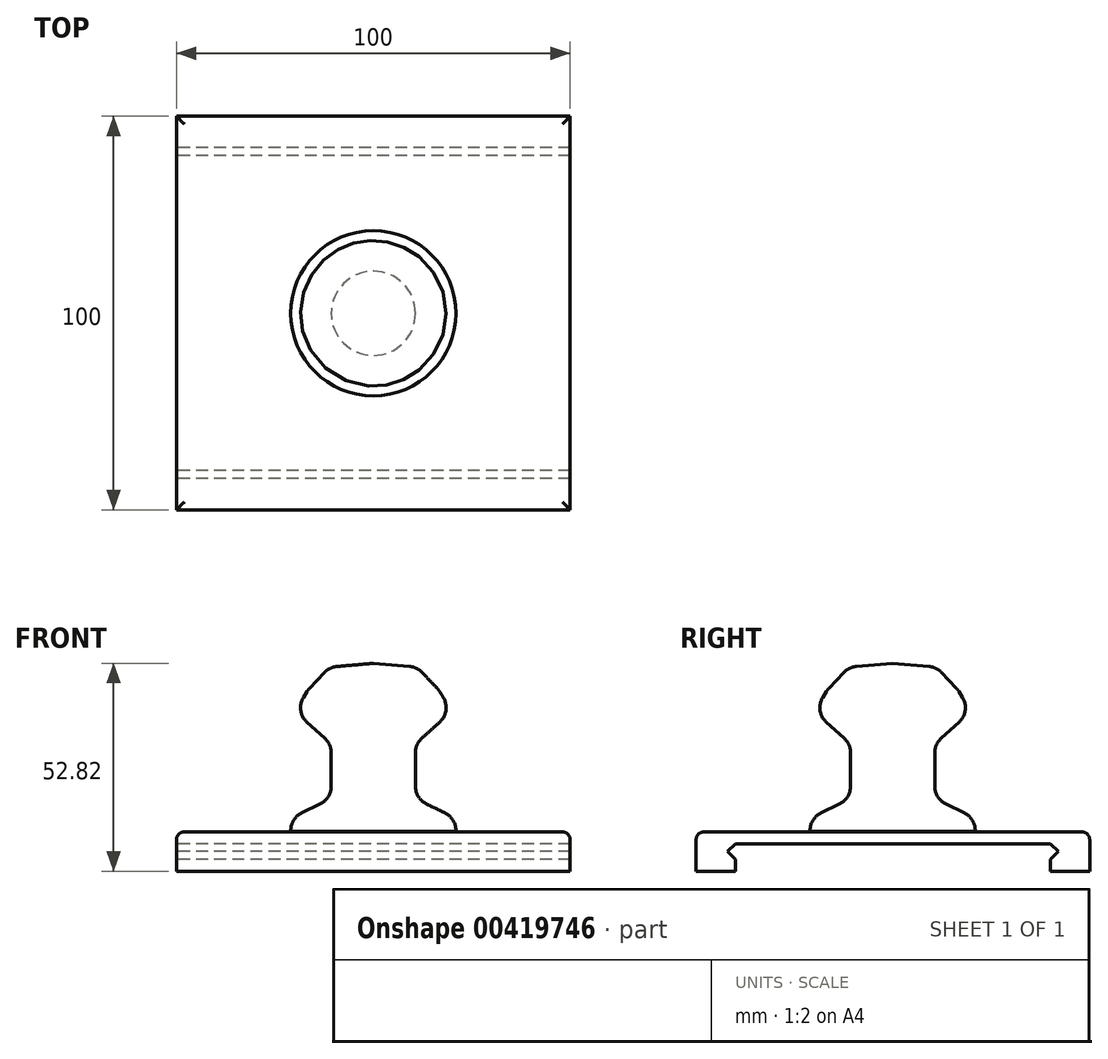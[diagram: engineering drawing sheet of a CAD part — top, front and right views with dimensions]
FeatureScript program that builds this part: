
annotation { "Feature Type Name" : "Feature", "Feature Type Description" : "" }
export const myFeature = defineFeature(function(context is Context, id is Id, definition is map)
    precondition{}
    {
        {
            var Q0;
            Q0=qCreatedBy(makeId("Right.planeOp"),FACE);
            var sketch = newSketch(context, id + "F0", { "sketchPlane" : qUnion([Q0])});
            skLineSegment(sketch, "E0", {"start": v(-49.94, -0.09) * mm, "end": v(50.06, -0.09) * mm});
            skLineSegment(sketch, "E1", {"start": v(50.06, -0.09) * mm, "end": v(50.06, -10.09) * mm});
            skLineSegment(sketch, "E2", {"start": v(50.06, -10.09) * mm, "end": v(40.06, -10.09) * mm});
            skLineSegment(sketch, "E3", {"start": v(40.06, -10.09) * mm, "end": v(40.06, -7.09) * mm});
            skLineSegment(sketch, "E4", {"start": v(40.06, -3.09) * mm, "end": v(-39.94, -3.09) * mm});
            skLineSegment(sketch, "E5", {"start": v(-39.94, -7.09) * mm, "end": v(-39.94, -10.09) * mm});
            skLineSegment(sketch, "E6", {"start": v(-39.94, -10.09) * mm, "end": v(-49.94, -10.09) * mm});
            skLineSegment(sketch, "E7", {"start": v(-49.94, -10.09) * mm, "end": v(-49.94, -0.09) * mm});
            skLineSegment(sketch, "E8", {"start": v(-41.94, -5.09) * mm, "end": v(-39.94, -7.09) * mm});
            skLineSegment(sketch, "E9", {"start": v(-39.94, -3.09) * mm, "end": v(-41.94, -5.09) * mm});
            skLineSegment(sketch, "E10", {"start": v(40.06, -3.09) * mm, "end": v(42.06, -5.09) * mm});
            skLineSegment(sketch, "E11", {"start": v(42.06, -5.09) * mm, "end": v(40.06, -7.09) * mm});
            skPoint(sketch, "E12", {"position": v(0.06, 0) * mm});
            skPoint(sketch, "E12.positionSnap0", {"position": v(0.06, -0.09) * mm});
            skSolve(sketch);
        }
        {
            var Q0;
            Q0=makeQuery(id+"F0.imprint","IMPRINT",FACE,{"disambiguationData":[TD([[makeQuery(id+"F0.imprint","IMPRINT",EDGE,{"derivedFrom":sQuery(id+"F0.wireOp",EDGE,"E0")}),-1.0]])]});
            extrude(context, id + "F1", {"entities" : qUnion([Q0]), "depth" : 50 * mm});
        }
        {
            var Q0;
            Q0=qCreatedBy(makeId("Right.planeOp"),FACE);
            var sketch = newSketch(context, id + "F2", { "sketchPlane" : qUnion([Q0])});
            skLineSegment(sketch, "E13", {"start": v(0, 42.73) * mm, "end": v(0, 0) * mm});
            skLineSegment(sketch, "E14", {"start": v(0, 0) * mm, "end": v(20.99, 0) * mm});
            skLineSegment(sketch, "E15", {"start": v(20.99, 0) * mm, "end": v(20.99, 0.24) * mm});
            skLineSegment(sketch, "E16", {"start": v(18.18, 4.73) * mm, "end": v(13.5, 7) * mm});
            skLineSegment(sketch, "E17", {"start": v(10.7, 11.5) * mm, "end": v(10.7, 20) * mm});
            skLineSegment(sketch, "E18", {"start": v(12.35, 23.72) * mm, "end": v(16.84, 27.76) * mm});
            skLineSegment(sketch, "E19", {"start": v(17.75, 34.1) * mm, "end": v(16.86, 35.55) * mm});
            skLineSegment(sketch, "E20", {"start": v(16.22, 36.38) * mm, "end": v(12.42, 40.39) * mm});
            skLineSegment(sketch, "E21", {"start": v(9.22, 41.93) * mm, "end": v(0, 42.73) * mm});
            skPoint(sketch, "E22.visualSharp", {"position": v(11.11, 41.77) * mm});
            skArc(sketch, "E22.filletArc", {"start": v(12.42, 40.39) * mm, "mid": v(10.96, 41.45) * mm, "end": v(9.22, 41.93) * mm});
            skArc(sketch, "E23.filletArc", {"start": v(16.86, 35.55) * mm, "mid": v(16.56, 35.98) * mm, "end": v(16.22, 36.38) * mm});
            skPoint(sketch, "E24.visualSharp", {"position": v(19.93, 30.55) * mm});
            skArc(sketch, "E24.filletArc", {"start": v(16.84, 27.76) * mm, "mid": v(18.44, 30.76) * mm, "end": v(17.75, 34.1) * mm});
            skPoint(sketch, "E25.visualSharp", {"position": v(10.7, 22.23) * mm});
            skArc(sketch, "E25.filletArc", {"start": v(12.35, 23.72) * mm, "mid": v(11.13, 22.04) * mm, "end": v(10.7, 20) * mm});
            skPoint(sketch, "E26.visualSharp", {"position": v(10.7, 8.38) * mm});
            skArc(sketch, "E26.filletArc", {"start": v(10.7, 11.5) * mm, "mid": v(11.45, 8.85) * mm, "end": v(13.5, 7) * mm});
            skPoint(sketch, "E27.visualSharp", {"position": v(20.99, 3.36) * mm});
            skArc(sketch, "E27.filletArc", {"start": v(20.99, 0.24) * mm, "mid": v(20.22, 2.89) * mm, "end": v(18.18, 4.73) * mm});
            skSolve(sketch);
        }
        {
            var Q0;
            Q0 = qSketchRegion(id + "F0", true);
            extrude(context, id + "F3", {"entities" : qUnion([Q0]), "operationType" : NewBodyOperationType.ADD, "depth" : -50 * mm});
        }
        {
            var Q0;
            Q0 = qSketchRegion(id + "F2", true);
            var Q1;
            Q1=sQuery(id+"F2.wireOp",EDGE,"E13");
            revolve(context, id + "F4", {"entities" : qUnion([Q0]), "axis" : qUnion([Q1]), "revolveType" : RevolveType.FULL});
        }
        {
            var Q0;
            Q0=makeQuery(id+"F3.opExtrude","CAP_EDGE",EDGE,{"disambiguationData":[OSD([sQuery(id+"F0.wireOp",EDGE,"E0")])],"isStart":false});
            var Q1;
            {var subQ0=sQuery(id+"F0.wireOp",EDGE,"E7");var subQ1=sQuery(id+"F0.wireOp",EDGE,"E0");Q1=makeQuery(id+"F3.boolean.opBoolean","MERGE",EDGE,{"derivedFrom":[makeQuery(id+"F1.opExtrude","SWEPT_EDGE",EDGE,{"disambiguationData":[OSD([subQ1,subQ0])]}),makeQuery(id+"F3.opExtrude","SWEPT_EDGE",EDGE,{"disambiguationData":[OSD([subQ1,subQ0])]})]});}
            var Q2;
            Q2=makeQuery(id+"F1.opExtrude","CAP_EDGE",EDGE,{"disambiguationData":[OSD([sQuery(id+"F0.wireOp",EDGE,"E0")])],"isStart":false});
            var Q3;
            {var subQ0=sQuery(id+"F0.wireOp",EDGE,"E1");var subQ1=sQuery(id+"F0.wireOp",EDGE,"E0");Q3=makeQuery(id+"F3.boolean.opBoolean","MERGE",EDGE,{"derivedFrom":[makeQuery(id+"F1.opExtrude","SWEPT_EDGE",EDGE,{"disambiguationData":[OSD([subQ1,subQ0])]}),makeQuery(id+"F3.opExtrude","SWEPT_EDGE",EDGE,{"disambiguationData":[OSD([subQ1,subQ0])]})]});}
            fillet(context, id + "F5", {"entities" : qUnion([Q0, Q1, Q2, Q3]), "radius" : 2 * mm, "tangentPropagation" : true, "allowEdgeOverflow" : false});
        }
    });
